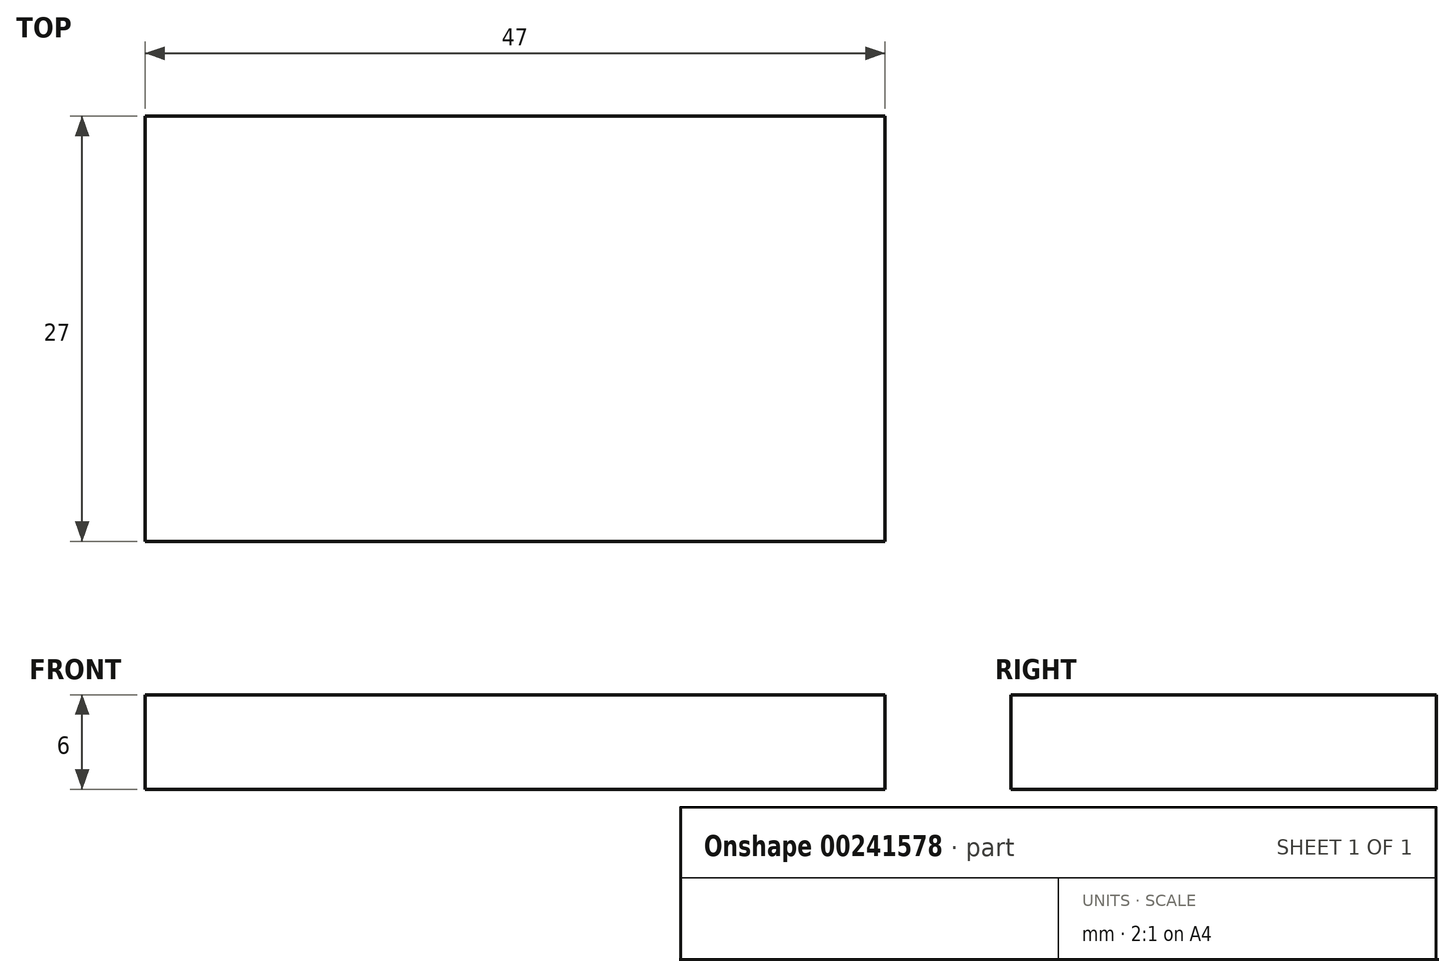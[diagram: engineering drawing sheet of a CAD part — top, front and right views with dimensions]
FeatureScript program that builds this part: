
annotation { "Feature Type Name" : "Feature", "Feature Type Description" : "" }
export const myFeature = defineFeature(function(context is Context, id is Id, definition is map)
    precondition{}
    {
        {
            var Q0;
            Q0=qCreatedBy(makeId("Top.planeOp"),FACE);
            var sketch = newSketch(context, id + "F0", { "sketchPlane" : qUnion([Q0])});
            skLineSegment(sketch, "E0.bottom", {"start": v(23.5, 13.5) * mm, "end": v(-23.5, 13.5) * mm});
            skLineSegment(sketch, "E0.top", {"start": v(23.5, -13.5) * mm, "end": v(-23.5, -13.5) * mm});
            skLineSegment(sketch, "E0.left", {"start": v(23.5, 13.5) * mm, "end": v(23.5, -13.5) * mm});
            skLineSegment(sketch, "E0.right", {"start": v(-23.5, 13.5) * mm, "end": v(-23.5, -13.5) * mm});
            skPoint(sketch, "E0.middle", {"position": v(0, 0) * mm});
            skSolve(sketch);
        }
        {
            var Q0;
            Q0 = qSketchRegion(id + "F0", true);
            extrude(context, id + "F1", {"entities" : qUnion([Q0]), "depth" : 6 * mm});
        }
    });
